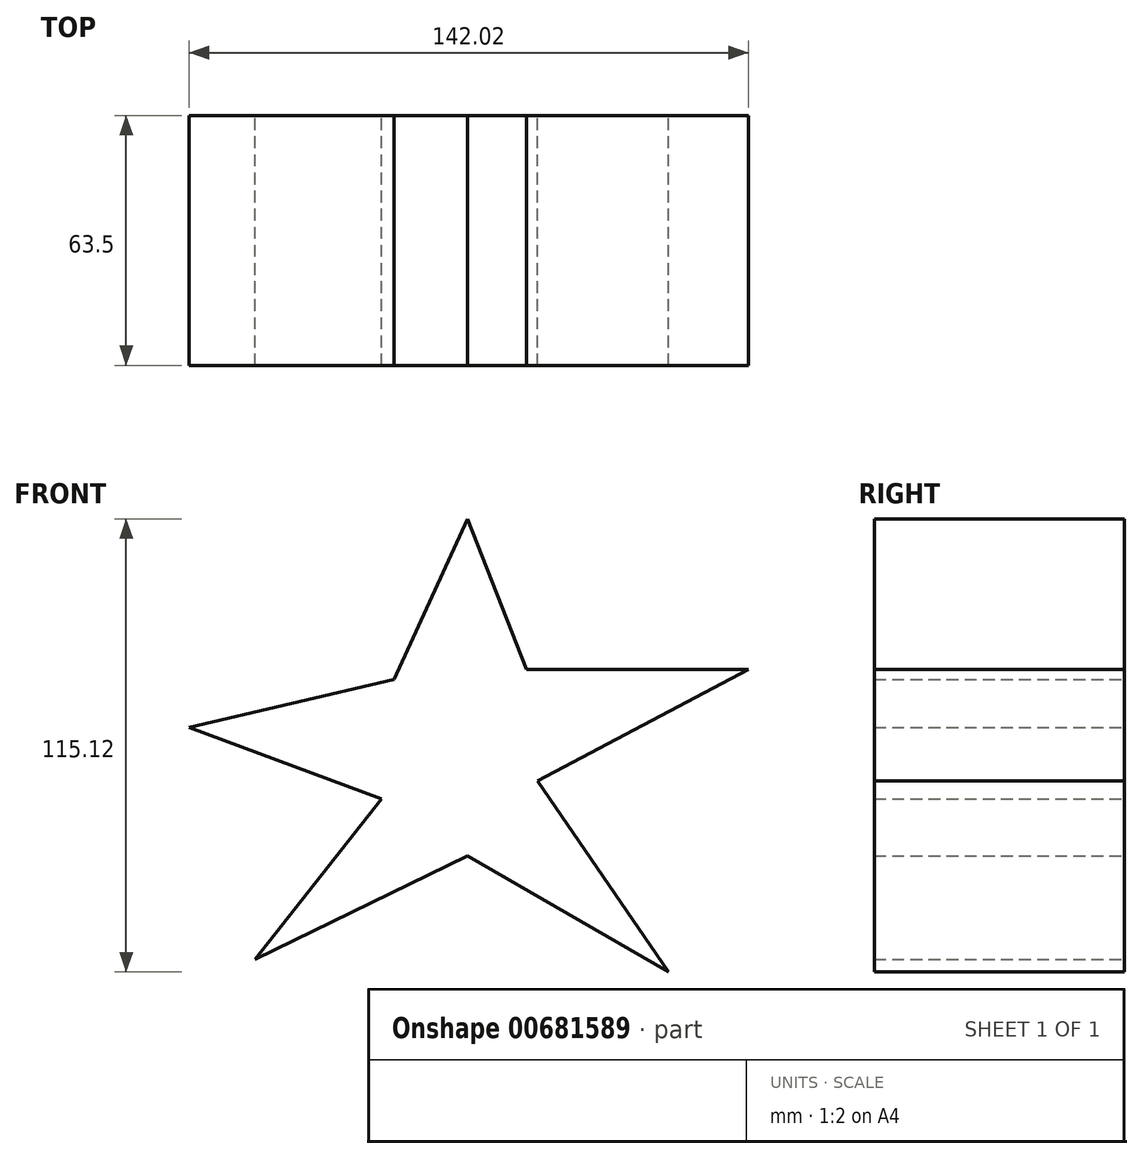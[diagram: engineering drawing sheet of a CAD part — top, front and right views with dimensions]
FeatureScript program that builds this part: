
annotation { "Feature Type Name" : "Feature", "Feature Type Description" : "" }
export const myFeature = defineFeature(function(context is Context, id is Id, definition is map)
    precondition{}
    {
        {
            var Q0;
            Q0=qCreatedBy(makeId("Front.planeOp"),FACE);
            var sketch = newSketch(context, id + "F0", { "sketchPlane" : qUnion([Q0])});
            skLineSegment(sketch, "E0", {"start": v(0, 77.23) * mm, "end": v(14.9, 39.05) * mm});
            skLineSegment(sketch, "E1", {"start": v(14.9, 39.05) * mm, "end": v(71.3, 39.05) * mm});
            skLineSegment(sketch, "E2", {"start": v(71.3, 39.05) * mm, "end": v(17.79, 10.7) * mm});
            skLineSegment(sketch, "E3", {"start": v(17.79, 10.7) * mm, "end": v(51.05, -37.9) * mm});
            skLineSegment(sketch, "E4", {"start": v(51.05, -37.9) * mm, "end": v(0, -8.39) * mm});
            skLineSegment(sketch, "E5", {"start": v(0, -8.39) * mm, "end": v(-53.94, -34.7) * mm});
            skLineSegment(sketch, "E6", {"start": v(-53.94, -34.7) * mm, "end": v(-21.84, 6.07) * mm});
            skLineSegment(sketch, "E7", {"start": v(-21.84, 6.07) * mm, "end": v(-70.72, 24.3) * mm});
            skLineSegment(sketch, "E8", {"start": v(-70.72, 24.3) * mm, "end": v(-18.66, 36.44) * mm});
            skLineSegment(sketch, "E9", {"start": v(-18.66, 36.44) * mm, "end": v(0, 77.23) * mm});
            skSolve(sketch);
        }
        {
            var Q0;
            Q0=makeQuery(id+"F0.imprint","IMPRINT",FACE,{"disambiguationData":[TD([[makeQuery(id+"F0.imprint","IMPRINT",EDGE,{"derivedFrom":sQuery(id+"F0.wireOp",EDGE,"E0")}),-1.0]])]});
            extrude(context, id + "F1", {"entities" : qUnion([Q0]), "depth" : 63.5 * mm, "offsetDistance" : 25.4 * mm});
        }
    });
